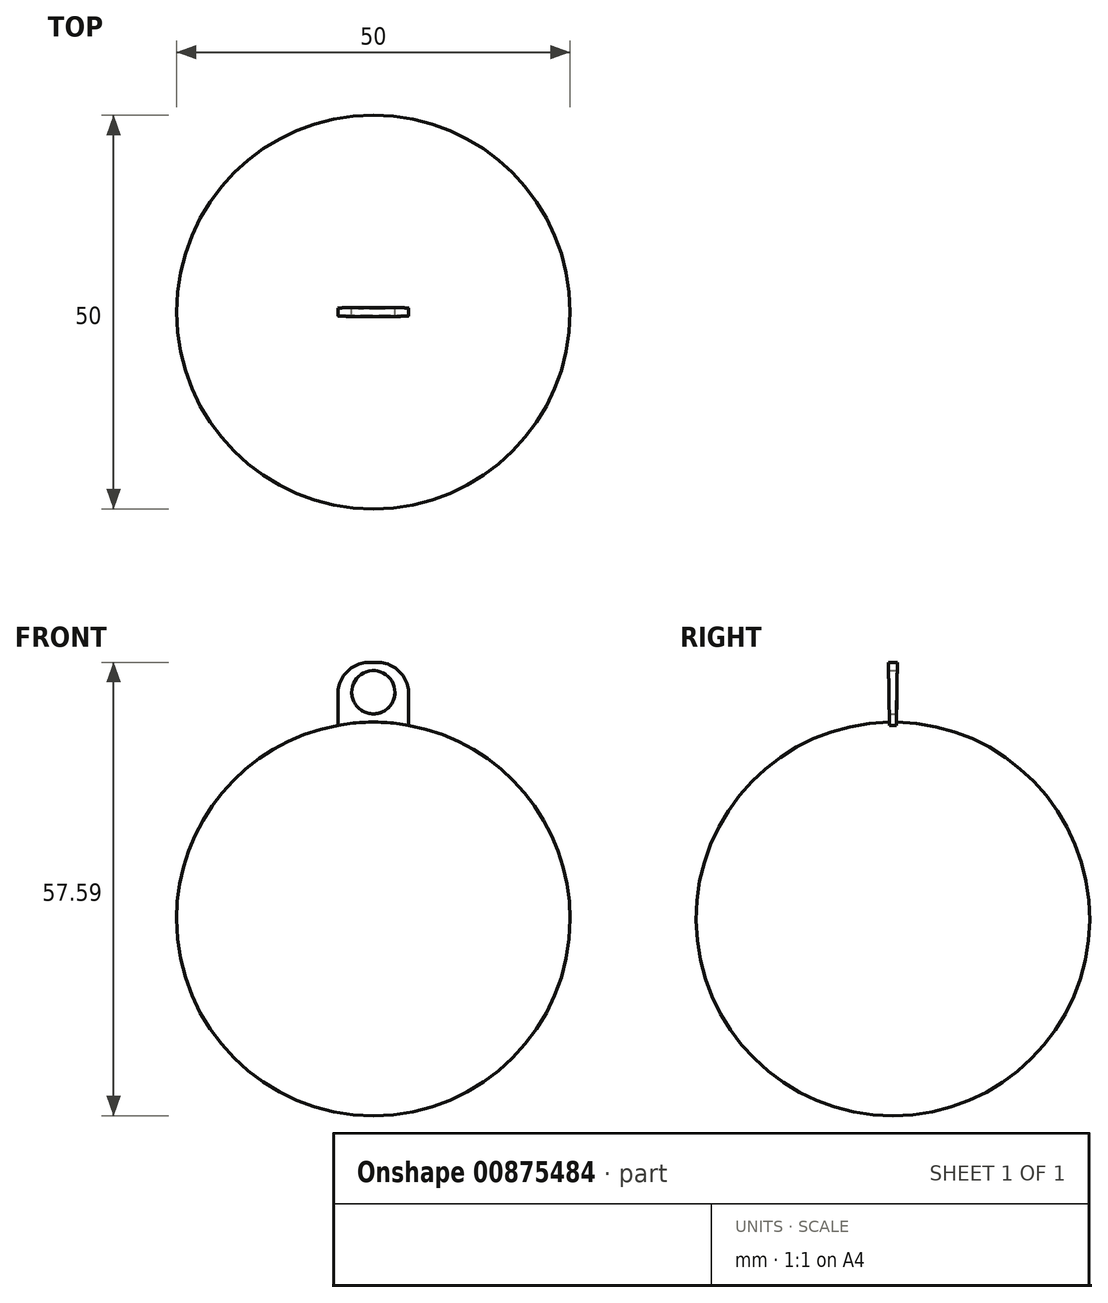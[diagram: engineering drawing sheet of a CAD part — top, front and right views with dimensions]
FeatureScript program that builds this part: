
annotation { "Feature Type Name" : "Feature", "Feature Type Description" : "" }
export const myFeature = defineFeature(function(context is Context, id is Id, definition is map)
    precondition{}
    {
        {
            var Q0;
            Q0=qCreatedBy(makeId("Front.planeOp"),FACE);
            var sketch = newSketch(context, id + "F0", { "sketchPlane" : qUnion([Q0])});
            skArc(sketch, "E0", {"start": v(25, 0) * mm, "mid": v(0, 25) * mm, "end": v(-25, 0) * mm});
            skLineSegment(sketch, "E1", {"start": v(-25, 0) * mm, "end": v(25, 0) * mm});
            skSolve(sketch);
        }
        {
            var Q0;
            Q0=qCreatedBy(makeId("Front.planeOp"),FACE);
            var sketch = newSketch(context, id + "F1", { "sketchPlane" : qUnion([Q0])});
            skArc(sketch, "E2", {"start": v(4.5, 24.6) * mm, "mid": v(0, 25) * mm, "end": v(-4.5, 24.6) * mm});
            skLineSegment(sketch, "E3", {"start": v(0, 25) * mm, "end": v(0, 32.6) * mm, "construction": true});
            skLineSegment(sketch, "E4", {"start": v(0, 32.6) * mm, "end": v(-0.5, 32.6) * mm});
            skLineSegment(sketch, "E5", {"start": v(-4.5, 28.6) * mm, "end": v(-4.5, 24.6) * mm});
            skPoint(sketch, "E6.visualSharp", {"position": v(-4.5, 32.6) * mm});
            skArc(sketch, "E6.filletArc", {"start": v(-0.5, 32.6) * mm, "mid": v(-3.33, 31.42) * mm, "end": v(-4.5, 28.6) * mm});
            skLineSegment(sketch, "E7.MirrorCS", {"start": v(0, 32.6) * mm, "end": v(0.5, 32.6) * mm});
            skArc(sketch, "E8.MirrorCS", {"start": v(0.5, 32.6) * mm, "mid": v(3.33, 31.42) * mm, "end": v(4.5, 28.6) * mm});
            skLineSegment(sketch, "E9.MirrorCS", {"start": v(4.5, 28.6) * mm, "end": v(4.5, 24.6) * mm});
            skCircle(sketch, "E10", {"center": v(0, 28.8) * mm, "radius": 2.75 * mm});
            skSolve(sketch);
        }
        {
            var Q0;
            Q0=makeQuery(id+"F1.imprint","IMPRINT",FACE,{"disambiguationData":[TD([[makeQuery(id+"F1.imprint","IMPRINT",EDGE,{"derivedFrom":sQuery(id+"F1.wireOp",EDGE,"E2")}),-1.0]])]});
            var Q1;
            Q1=sQuery(id+"F0.wireOp",EDGE,"E1");
            revolve(context, id + "F2", {"surfaceOperationType" : NewSurfaceOperationType.NEW, "entities" : qUnion([Q0]), "axis" : qUnion([Q1]), "revolveType" : RevolveType.TWO_DIRECTIONS, "angle" : 1 * degree, "angleBack" : 359 * degree});
        }
        {
            var Q0;
            Q0=qCreatedBy(makeId("Front.planeOp"),FACE);
            var sketch = newSketch(context, id + "F3", { "sketchPlane" : qUnion([Q0])});
            skLineSegment(sketch, "E11", {"start": v(-75.8, 0) * mm, "end": v(74.66, 0) * mm});
            skSolve(sketch);
        }
        {
            var Q0;
            Q0 = qSketchRegion(id + "F0", true);
            var Q1;
            Q1=sQuery(id+"F3.wireOp",EDGE,"E11");
            revolve(context, id + "F4", {"operationType" : NewBodyOperationType.ADD, "surfaceOperationType" : NewSurfaceOperationType.NEW, "entities" : qUnion([Q0]), "axis" : qUnion([Q1]), "revolveType" : RevolveType.FULL});
        }
    });
